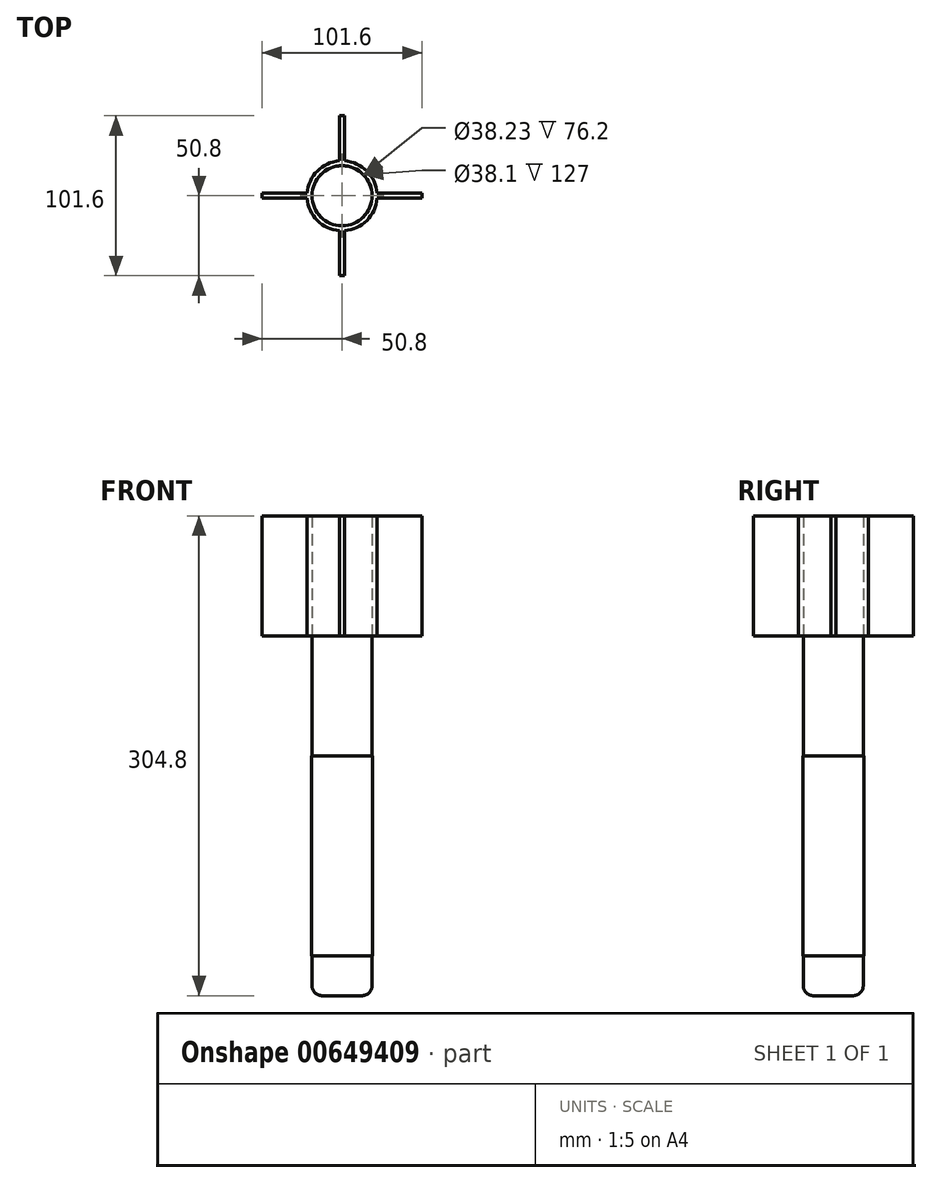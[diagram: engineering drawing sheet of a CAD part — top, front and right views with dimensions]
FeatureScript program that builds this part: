
annotation { "Feature Type Name" : "Feature", "Feature Type Description" : "" }
export const myFeature = defineFeature(function(context is Context, id is Id, definition is map)
    precondition{}
    {
        {
            var Q0;
            Q0=qCreatedBy(makeId("Top.planeOp"),FACE);
            var sketch = newSketch(context, id + "F0", { "sketchPlane" : qUnion([Q0])});
            skCircle(sketch, "E0", {"center": v(0, 0) * mm, "radius": 19.05 * mm});
            skSolve(sketch);
        }
        {
            var Q0;
            Q0 = qSketchRegion(id + "F0", true);
            extrude(context, id + "F1", {"entities" : qUnion([Q0]), "depth" : 152.4 * mm, "offsetDistance" : 25.4 * mm, "hasSecondDirection" : true, "secondDirectionOppositeDirection" : true, "secondDirectionDepth" : 152.4 * mm});
        }
        {
            var Q0;
            Q0=qCreatedBy(makeId("Top.planeOp"),FACE);
            var sketch = newSketch(context, id + "F2", { "sketchPlane" : qUnion([Q0])});
            skCircle(sketch, "E1", {"center": v(0, 0) * mm, "radius": 22.23 * mm});
            skLineSegment(sketch, "E2.bottom", {"start": v(1.59, 50.8) * mm, "end": v(-1.59, 50.8) * mm});
            skLineSegment(sketch, "E2.top", {"start": v(1.59, 19.05) * mm, "end": v(-1.59, 19.05) * mm});
            skLineSegment(sketch, "E2.left", {"start": v(1.59, 50.8) * mm, "end": v(1.59, 19.05) * mm});
            skLineSegment(sketch, "E2.right", {"start": v(-1.59, 50.8) * mm, "end": v(-1.59, 19.05) * mm});
            skPoint(sketch, "E2.middle", {"position": v(0, 34.92) * mm});
            skLineSegment(sketch, "E3.bottom", {"start": v(50.8, -1.59) * mm, "end": v(19.05, -1.59) * mm});
            skLineSegment(sketch, "E3.top", {"start": v(50.8, 1.59) * mm, "end": v(19.05, 1.59) * mm});
            skLineSegment(sketch, "E3.left", {"start": v(50.8, -1.59) * mm, "end": v(50.8, 1.59) * mm});
            skLineSegment(sketch, "E3.right", {"start": v(19.05, -1.59) * mm, "end": v(19.05, 1.59) * mm});
            skPoint(sketch, "E3.middle", {"position": v(34.92, 0) * mm});
            skLineSegment(sketch, "E4.bottom", {"start": v(1.59, -50.8) * mm, "end": v(-1.59, -50.8) * mm});
            skLineSegment(sketch, "E4.top", {"start": v(1.59, -19.05) * mm, "end": v(-1.59, -19.05) * mm});
            skLineSegment(sketch, "E4.left", {"start": v(1.59, -50.8) * mm, "end": v(1.59, -19.05) * mm});
            skLineSegment(sketch, "E4.right", {"start": v(-1.59, -50.8) * mm, "end": v(-1.59, -19.05) * mm});
            skPoint(sketch, "E4.middle", {"position": v(0, -34.92) * mm});
            skLineSegment(sketch, "E5.bottom", {"start": v(-50.8, -1.59) * mm, "end": v(-19.05, -1.59) * mm});
            skLineSegment(sketch, "E5.top", {"start": v(-50.8, 1.59) * mm, "end": v(-19.05, 1.59) * mm});
            skLineSegment(sketch, "E5.left", {"start": v(-50.8, -1.59) * mm, "end": v(-50.8, 1.59) * mm});
            skLineSegment(sketch, "E5.right", {"start": v(-19.05, -1.59) * mm, "end": v(-19.05, 1.59) * mm});
            skPoint(sketch, "E5.middle", {"position": v(-34.92, 0) * mm});
            skCircle(sketch, "E6", {"center": v(0, 0) * mm, "radius": 19.12 * mm});
            skSolve(sketch);
        }
        {
            var Q0;
            Q0 = qSketchRegion(id + "F2", true);
            extrude(context, id + "F3", {"entities" : qUnion([Q0]), "depth" : 152.4 * mm, "offsetDistance" : 25.4 * mm, "hasSecondDirection" : true, "secondDirectionOppositeDirection" : false, "secondDirectionDepth" : 76.2 * mm});
        }
        {
            var Q0;
            Q0=makeQuery(id+"F1.opExtrude","CAP_FACE",FACE,{"disambiguationData":[OSD([sQuery(id+"F0.wireOp",EDGE,"E0")])],"isStart":true});
            fillet(context, id + "F4", {"entities" : qUnion([Q0]), "radius" : 6.35 * mm, "tangentPropagation" : true, "allowEdgeOverflow" : false});
        }
        {
            var Q0;
            Q0=qCreatedBy(makeId("Top.planeOp"),FACE);
            var sketch = newSketch(context, id + "F5", { "sketchPlane" : qUnion([Q0])});
            skCircle(sketch, "E7", {"center": v(0, 0) * mm, "radius": 19.44 * mm});
            skCircle(sketch, "E8", {"center": v(0, 0) * mm, "radius": 19.05 * mm});
            skSolve(sketch);
        }
        {
            var Q0;
            Q0 = qSketchRegion(id + "F5", true);
            extrude(context, id + "F6", {"entities" : qUnion([Q0]), "oppositeDirection" : true, "depth" : 127 * mm, "offsetDistance" : 25.4 * mm});
        }
    });
